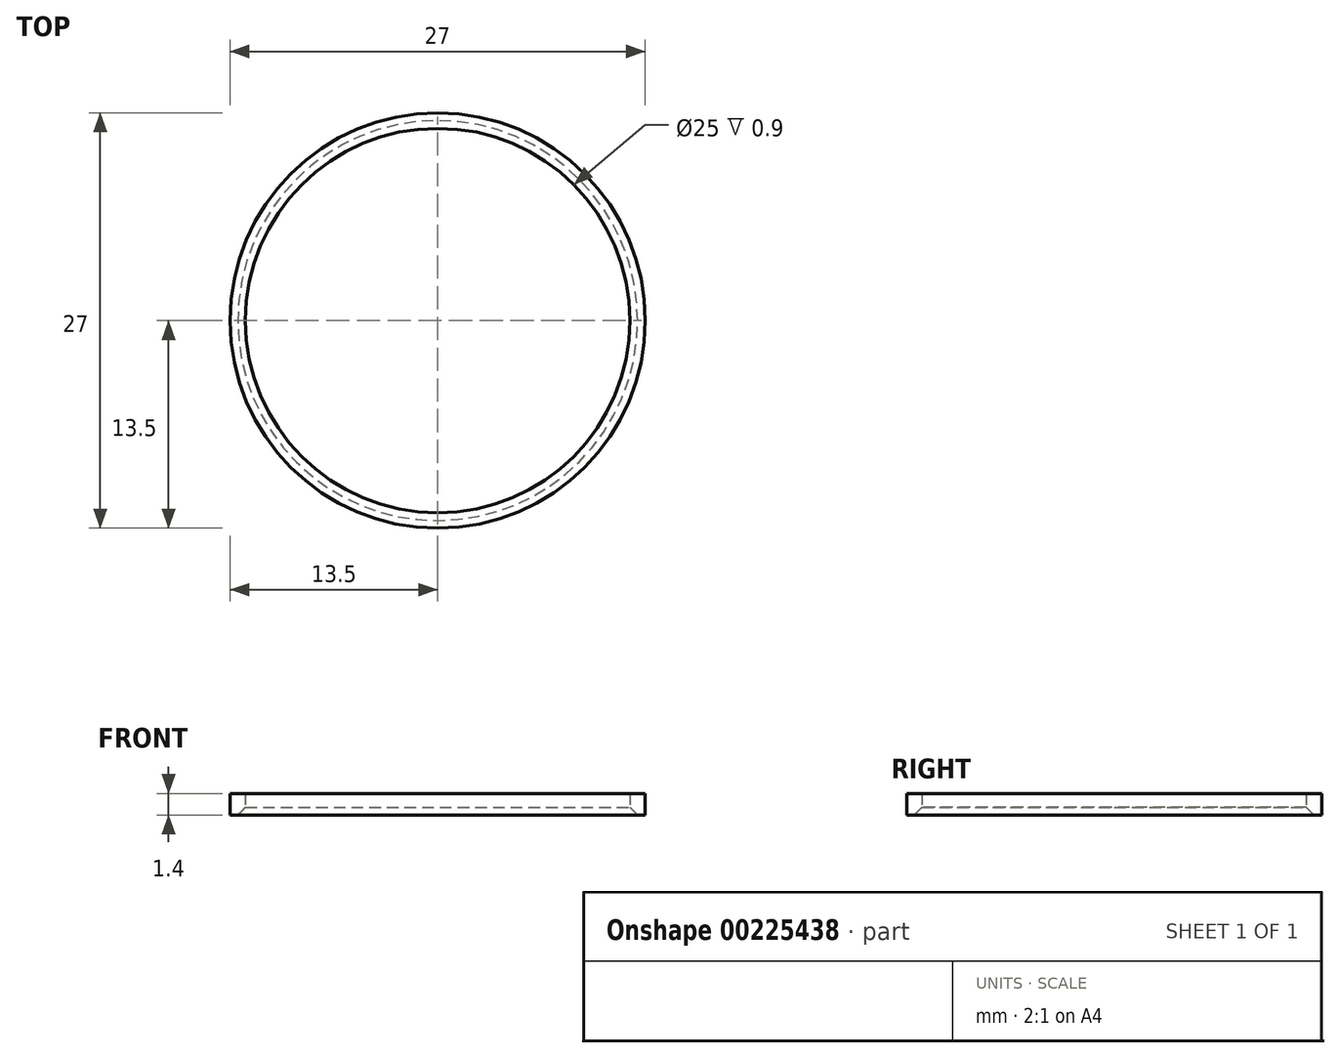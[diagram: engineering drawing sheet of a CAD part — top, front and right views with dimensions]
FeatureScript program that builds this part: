
annotation { "Feature Type Name" : "Feature", "Feature Type Description" : "" }
export const myFeature = defineFeature(function(context is Context, id is Id, definition is map)
    precondition{}
    {
        {
            var Q0;
            Q0=qCreatedBy(makeId("Front.planeOp"),FACE);
            var sketch = newSketch(context, id + "F0", { "sketchPlane" : qUnion([Q0])});
            skLineSegment(sketch, "E0", {"start": v(0, 0) * mm, "end": v(0, 9.64) * mm, "construction": true});
            skLineSegment(sketch, "E1", {"start": v(13.5, 0) * mm, "end": v(13.5, 1.4) * mm});
            skLineSegment(sketch, "E2", {"start": v(13.5, 1.4) * mm, "end": v(12.5, 1.4) * mm});
            skLineSegment(sketch, "E3", {"start": v(12.5, 1.4) * mm, "end": v(12.5, 0.5) * mm});
            skLineSegment(sketch, "E4", {"start": v(12.5, 0.5) * mm, "end": v(13, 0) * mm});
            skLineSegment(sketch, "E5", {"start": v(13, 0) * mm, "end": v(13.5, 0) * mm});
            skSolve(sketch);
        }
        {
            var Q0;
            Q0=makeQuery(id+"F0.imprint","IMPRINT",FACE,{"disambiguationData":[TD([[makeQuery(id+"F0.imprint","IMPRINT",EDGE,{"derivedFrom":sQuery(id+"F0.wireOp",EDGE,"E1")}),1.0]])]});
            var Q1;
            Q1=sQuery(id+"F0.wireOp",EDGE,"E0");
            revolve(context, id + "F1", {"entities" : qUnion([Q0]), "axis" : qUnion([Q1]), "revolveType" : RevolveType.FULL});
        }
    });
